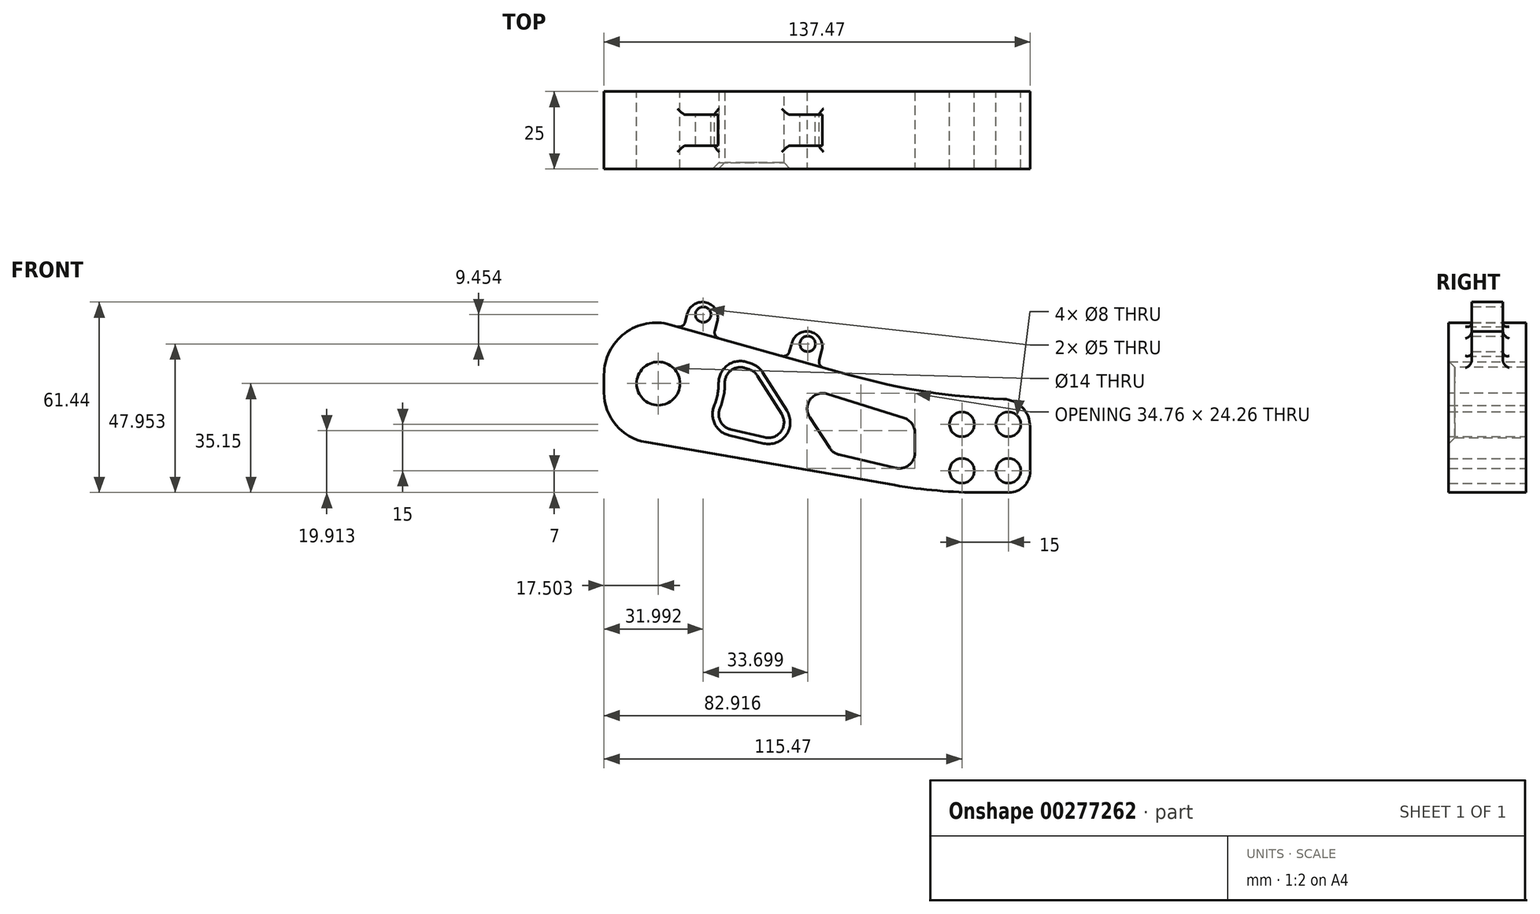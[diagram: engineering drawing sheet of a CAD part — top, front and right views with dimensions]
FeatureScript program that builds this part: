
annotation { "Feature Type Name" : "Feature", "Feature Type Description" : "" }
export const myFeature = defineFeature(function(context is Context, id is Id, definition is map)
    precondition{}
    {
        {
            var Q0;
            Q0=qCreatedBy(makeId("Front.planeOp"),FACE);
            var sketch = newSketch(context, id + "F0", { "sketchPlane" : qUnion([Q0])});
            skLineSegment(sketch, "E0.bottom", {"start": v(15, 15) * mm, "end": v(-15, 15) * mm});
            skLineSegment(sketch, "E0.top", {"start": v(15, -15) * mm, "end": v(-15, -15) * mm});
            skLineSegment(sketch, "E0.left", {"start": v(15, 15) * mm, "end": v(15, -15) * mm});
            skLineSegment(sketch, "E0.right", {"start": v(-15, 15) * mm, "end": v(-15, -15) * mm});
            skPoint(sketch, "E0.middle", {"position": v(0, 0) * mm});
            skCircle(sketch, "E1", {"center": v(-7, 7) * mm, "radius": 4 * mm});
            skCircle(sketch, "E2.0.1.0", {"center": v(-7, -8) * mm, "radius": 4 * mm});
            skCircle(sketch, "E2.1.0.0", {"center": v(8, 7) * mm, "radius": 4 * mm});
            skCircle(sketch, "E2.1.1.0", {"center": v(8, -8) * mm, "radius": 4 * mm});
            skLineSegment(sketch, "E2.direction1", {"start": v(-7, 7) * mm, "end": v(8, 7) * mm, "construction": true});
            skLineSegment(sketch, "E2.direction2", {"start": v(-7, 7) * mm, "end": v(-7, -8) * mm, "construction": true});
            skLineSegment(sketch, "E3", {"start": v(-15, 15) * mm, "end": v(-122.47, 45.15) * mm});
            skLineSegment(sketch, "E4", {"start": v(-122.47, 45.15) * mm, "end": v(-122.47, 3.55) * mm});
            skLineSegment(sketch, "E5", {"start": v(-122.47, 3.55) * mm, "end": v(-15, -15) * mm});
            skCircle(sketch, "E6", {"center": v(-104.97, 20.15) * mm, "radius": 7 * mm});
            skLineSegment(sketch, "E7", {"start": v(-96.91, 37.98) * mm, "end": v(-94.21, 47.6) * mm});
            skLineSegment(sketch, "E8", {"start": v(-94.21, 47.6) * mm, "end": v(-84.58, 44.9) * mm});
            skLineSegment(sketch, "E9", {"start": v(-84.58, 44.9) * mm, "end": v(-87.28, 35.28) * mm});
            skLineSegment(sketch, "E10", {"start": v(-87.28, 35.28) * mm, "end": v(-96.91, 37.98) * mm});
            skLineSegment(sketch, "E11", {"start": v(-63.21, 28.53) * mm, "end": v(-60.51, 38.15) * mm});
            skLineSegment(sketch, "E12", {"start": v(-60.51, 38.15) * mm, "end": v(-50.88, 35.45) * mm});
            skLineSegment(sketch, "E13", {"start": v(-50.88, 35.45) * mm, "end": v(-53.59, 25.83) * mm});
            skSolve(sketch);
        }
        {
            var Q0;
            Q0 = qSketchRegion(id + "F0", true);
            extrude(context, id + "F1", {"entities" : qUnion([Q0]), "depth" : 25 * mm});
        }
        {
            var Q0;
            Q0=makeQuery(id+"F1.opExtrude","SWEPT_EDGE",EDGE,{"disambiguationData":[OSD([sQuery(id+"F0.wireOp",EDGE,"E3"),sQuery(id+"F0.wireOp",EDGE,"E4")])]});
            fillet(context, id + "F2", {"entities" : qUnion([Q0]), "radius" : 16.78 * mm, "tangentPropagation" : true, "allowEdgeOverflow" : false});
        }
        {
            var Q0;
            Q0=makeQuery(id+"F1.opExtrude","SWEPT_EDGE",EDGE,{"disambiguationData":[OSD([sQuery(id+"F0.wireOp",EDGE,"E4"),sQuery(id+"F0.wireOp",EDGE,"E5")])]});
            fillet(context, id + "F3", {"entities" : qUnion([Q0]), "radius" : 16.27 * mm, "tangentPropagation" : true, "allowEdgeOverflow" : false});
        }
        {
            var Q0;
            Q0=makeQuery(id+"F1.opExtrude","SWEPT_EDGE",EDGE,{"disambiguationData":[OSD([sQuery(id+"F0.wireOp",EDGE,"E0.bottom"),sQuery(id+"F0.wireOp",EDGE,"E0.right"),sQuery(id+"F0.wireOp",EDGE,"E3")])]});
            fillet(context, id + "F4", {"entities" : qUnion([Q0]), "radius" : 212.2 * mm, "tangentPropagation" : true, "allowEdgeOverflow" : false});
        }
        {
            var Q0;
            Q0=makeQuery(id+"F1.opExtrude","SWEPT_EDGE",EDGE,{"disambiguationData":[OSD([sQuery(id+"F0.wireOp",EDGE,"E0.top"),sQuery(id+"F0.wireOp",EDGE,"E0.right"),sQuery(id+"F0.wireOp",EDGE,"E5")])]});
            fillet(context, id + "F5", {"entities" : qUnion([Q0]), "radius" : 163.8 * mm, "tangentPropagation" : true, "allowEdgeOverflow" : false});
        }
        {
            var Q0;
            Q0=makeQuery(id+"F1.opExtrude","SWEPT_EDGE",EDGE,{"disambiguationData":[OSD([sQuery(id+"F0.wireOp",EDGE,"E0.bottom"),sQuery(id+"F0.wireOp",EDGE,"E0.left")])]});
            fillet(context, id + "F6", {"entities" : qUnion([Q0]), "radius" : 8.93 * mm, "tangentPropagation" : true, "allowEdgeOverflow" : false});
        }
        {
            var Q0;
            Q0=makeQuery(id+"F1.opExtrude","SWEPT_EDGE",EDGE,{"disambiguationData":[OSD([sQuery(id+"F0.wireOp",EDGE,"E0.top"),sQuery(id+"F0.wireOp",EDGE,"E0.left")])]});
            fillet(context, id + "F7", {"entities" : qUnion([Q0]), "radius" : 6.76 * mm, "tangentPropagation" : true, "allowEdgeOverflow" : false});
        }
        {
            var Q0;
            Q0=makeQuery(id+"F1.opExtrude","CAP_FACE",FACE,{"disambiguationData":[OSD([sQuery(id+"F0.wireOp",EDGE,"E0.bottom"),sQuery(id+"F0.wireOp",EDGE,"E0.top"),sQuery(id+"F0.wireOp",EDGE,"E0.left"),sQuery(id+"F0.wireOp",EDGE,"E1"),sQuery(id+"F0.wireOp",EDGE,"E2.0.1.0"),sQuery(id+"F0.wireOp",EDGE,"E2.1.0.0"),sQuery(id+"F0.wireOp",EDGE,"E2.1.1.0"),sQuery(id+"F0.wireOp",EDGE,"E3"),sQuery(id+"F0.wireOp",EDGE,"E4"),sQuery(id+"F0.wireOp",EDGE,"E5"),sQuery(id+"F0.wireOp",EDGE,"E6")])],"isStart":false});
            var sketch = newSketch(context, id + "F8", { "sketchPlane" : qUnion([Q0])});
            skLineSegment(sketch, "E14", {"start": v(-84.84, 27.64) * mm, "end": v(-73.97, 24.22) * mm});
            skLineSegment(sketch, "E15", {"start": v(-22.17, 7.92) * mm, "end": v(-22.17, -8.52) * mm});
            skLineSegment(sketch, "E16", {"start": v(-22.17, -8.52) * mm, "end": v(-48.58, -2.35) * mm});
            skArc(sketch, "E17", {"start": v(-88.2, 6.9) * mm, "mid": v(-83.78, 16.83) * mm, "end": v(-84.84, 27.64) * mm});
            skLineSegment(sketch, "E18", {"start": v(-73.97, 24.22) * mm, "end": v(-58.64, 0) * mm});
            skLineSegment(sketch, "E19", {"start": v(-63.67, 20.98) * mm, "end": v(-48.58, -2.35) * mm});
            skLineSegment(sketch, "E20.trimOffspring", {"start": v(-63.67, 20.98) * mm, "end": v(-22.17, 7.92) * mm});
            skLineSegment(sketch, "E21.trimOffspring", {"start": v(-58.64, 0) * mm, "end": v(-88.2, 6.9) * mm});
            skSolve(sketch);
        }
        {
            var Q0;
            Q0 = qSketchRegion(id + "F8", true);
            extrude(context, id + "F9", {"entities" : qUnion([Q0]), "operationType" : NewBodyOperationType.REMOVE, "oppositeDirection" : true, "depth" : 25 * mm});
        }
        {
            var Q0;
            Q0=makeQuery(id+"F9.boolean.opBoolean","COPY",EDGE,{"derivedFrom":makeQuery(id+"F9.opExtrude","SWEPT_EDGE",EDGE,{"disambiguationData":[OSD([sQuery(id+"F8.wireOp",EDGE,"E17"),sQuery(id+"F8.wireOp",EDGE,"E21.trimOffspring")])]})});
            var Q1;
            Q1=makeQuery(id+"F9.boolean.opBoolean","COPY",EDGE,{"derivedFrom":makeQuery(id+"F9.opExtrude","SWEPT_EDGE",EDGE,{"disambiguationData":[OSD([sQuery(id+"F8.wireOp",EDGE,"E14"),sQuery(id+"F8.wireOp",EDGE,"E17")])]})});
            var Q2;
            Q2=makeQuery(id+"F9.boolean.opBoolean","COPY",EDGE,{"derivedFrom":makeQuery(id+"F9.opExtrude","SWEPT_EDGE",EDGE,{"disambiguationData":[OSD([sQuery(id+"F8.wireOp",EDGE,"E14"),sQuery(id+"F8.wireOp",EDGE,"E18")])]})});
            var Q3;
            Q3=makeQuery(id+"F9.boolean.opBoolean","COPY",EDGE,{"derivedFrom":makeQuery(id+"F9.opExtrude","SWEPT_EDGE",EDGE,{"disambiguationData":[OSD([sQuery(id+"F8.wireOp",EDGE,"E18"),sQuery(id+"F8.wireOp",EDGE,"E21.trimOffspring")])]})});
            var Q4;
            Q4=makeQuery(id+"F9.boolean.opBoolean","COPY",EDGE,{"derivedFrom":makeQuery(id+"F9.opExtrude","SWEPT_EDGE",EDGE,{"disambiguationData":[OSD([sQuery(id+"F8.wireOp",EDGE,"E19"),sQuery(id+"F8.wireOp",EDGE,"E20.trimOffspring")])]})});
            var Q5;
            Q5=makeQuery(id+"F9.boolean.opBoolean","COPY",EDGE,{"derivedFrom":makeQuery(id+"F9.opExtrude","SWEPT_EDGE",EDGE,{"disambiguationData":[OSD([sQuery(id+"F8.wireOp",EDGE,"E16"),sQuery(id+"F8.wireOp",EDGE,"E19")])]})});
            var Q6;
            Q6=makeQuery(id+"F9.boolean.opBoolean","COPY",EDGE,{"derivedFrom":makeQuery(id+"F9.opExtrude","SWEPT_EDGE",EDGE,{"disambiguationData":[OSD([sQuery(id+"F8.wireOp",EDGE,"E15"),sQuery(id+"F8.wireOp",EDGE,"E16")])]})});
            var Q7;
            Q7=makeQuery(id+"F9.boolean.opBoolean","COPY",EDGE,{"derivedFrom":makeQuery(id+"F9.opExtrude","SWEPT_EDGE",EDGE,{"disambiguationData":[OSD([sQuery(id+"F8.wireOp",EDGE,"E15"),sQuery(id+"F8.wireOp",EDGE,"E20.trimOffspring")])]})});
            fillet(context, id + "F10", {"entities" : qUnion([Q0, Q1, Q2, Q3, Q4, Q5, Q6, Q7]), "radius" : 5 * mm, "tangentPropagation" : true, "allowEdgeOverflow" : false});
        }
        {
            var Q0;
            Q0=makeQuery(id+"F10.opFillet","BLEND_EDGE",EDGE,{"blendedFrom":[makeQuery(id+"F9.boolean.opBoolean","COPY",EDGE,{"derivedFrom":makeQuery(id+"F9.opExtrude","SWEPT_EDGE",EDGE,{"disambiguationData":[OSD([sQuery(id+"F8.wireOp",EDGE,"E14"),sQuery(id+"F8.wireOp",EDGE,"E17")])]})}),makeQuery(id+"F1.opExtrude","CAP_FACE",FACE,{"disambiguationData":[OSD([sQuery(id+"F0.wireOp",EDGE,"E0.bottom"),sQuery(id+"F0.wireOp",EDGE,"E0.top"),sQuery(id+"F0.wireOp",EDGE,"E0.left"),sQuery(id+"F0.wireOp",EDGE,"E1"),sQuery(id+"F0.wireOp",EDGE,"E2.0.1.0"),sQuery(id+"F0.wireOp",EDGE,"E2.1.0.0"),sQuery(id+"F0.wireOp",EDGE,"E2.1.1.0"),sQuery(id+"F0.wireOp",EDGE,"E3"),sQuery(id+"F0.wireOp",EDGE,"E4"),sQuery(id+"F0.wireOp",EDGE,"E5"),sQuery(id+"F0.wireOp",EDGE,"E6")])],"isStart":false})],"blendedInto":[makeQuery(id+"F1.opExtrude","CAP_FACE",FACE,{"disambiguationData":[OSD([sQuery(id+"F0.wireOp",EDGE,"E0.bottom"),sQuery(id+"F0.wireOp",EDGE,"E0.top"),sQuery(id+"F0.wireOp",EDGE,"E0.left"),sQuery(id+"F0.wireOp",EDGE,"E1"),sQuery(id+"F0.wireOp",EDGE,"E2.0.1.0"),sQuery(id+"F0.wireOp",EDGE,"E2.1.0.0"),sQuery(id+"F0.wireOp",EDGE,"E2.1.1.0"),sQuery(id+"F0.wireOp",EDGE,"E3"),sQuery(id+"F0.wireOp",EDGE,"E4"),sQuery(id+"F0.wireOp",EDGE,"E5"),sQuery(id+"F0.wireOp",EDGE,"E6")])],"isStart":false})]});
            var Q1;
            Q1=makeQuery(id+"F9.boolean.opBoolean","COPY",EDGE,{"derivedFrom":makeQuery(id+"F9.opExtrude","CAP_EDGE",EDGE,{"disambiguationData":[OSD([sQuery(id+"F8.wireOp",EDGE,"E20.trimOffspring")])],"isStart":true})});
            var Q2;
            Q2=makeQuery(id+"F9.boolean.opBoolean","COPY",EDGE,{"derivedFrom":makeQuery(id+"F9.opExtrude","CAP_EDGE",EDGE,{"disambiguationData":[OSD([sQuery(id+"F8.wireOp",EDGE,"E20.trimOffspring")])],"isStart":false})});
            var Q3;
            Q3=makeQuery(id+"F9.boolean.opBoolean","COPY",EDGE,{"derivedFrom":makeQuery(id+"F9.opExtrude","CAP_EDGE",EDGE,{"disambiguationData":[OSD([sQuery(id+"F8.wireOp",EDGE,"E18")])],"isStart":false})});
            chamfer(context, id + "F11", {"entities" : qUnion([Q0, Q1, Q2, Q3]), "width" : 2 * mm, "tangentPropagation" : true});
        }
        {
            var Q0;
            Q0=makeQuery(id+"F1.opExtrude","CAP_FACE",FACE,{"disambiguationData":[OSD([sQuery(id+"F0.wireOp",EDGE,"E0.bottom"),sQuery(id+"F0.wireOp",EDGE,"E0.top"),sQuery(id+"F0.wireOp",EDGE,"E0.left"),sQuery(id+"F0.wireOp",EDGE,"E1"),sQuery(id+"F0.wireOp",EDGE,"E2.0.1.0"),sQuery(id+"F0.wireOp",EDGE,"E2.1.0.0"),sQuery(id+"F0.wireOp",EDGE,"E2.1.1.0"),sQuery(id+"F0.wireOp",EDGE,"E3"),sQuery(id+"F0.wireOp",EDGE,"E4"),sQuery(id+"F0.wireOp",EDGE,"E5"),sQuery(id+"F0.wireOp",EDGE,"E6"),sQuery(id+"F0.wireOp",EDGE,"E7"),sQuery(id+"F0.wireOp",EDGE,"E8"),sQuery(id+"F0.wireOp",EDGE,"E9"),sQuery(id+"F0.wireOp",EDGE,"E11"),sQuery(id+"F0.wireOp",EDGE,"E12"),sQuery(id+"F0.wireOp",EDGE,"E13")])],"isStart":false});
            var sketch = newSketch(context, id + "F12", { "sketchPlane" : qUnion([Q0])});
            skLineSegment(sketch, "E22", {"start": v(-60.51, 38.15) * mm, "end": v(-63.21, 28.53) * mm});
            skLineSegment(sketch, "E23", {"start": v(-63.21, 28.53) * mm, "end": v(-53.59, 25.83) * mm});
            skLineSegment(sketch, "E24", {"start": v(-53.59, 25.83) * mm, "end": v(-50.88, 35.45) * mm});
            skLineSegment(sketch, "E25", {"start": v(-50.88, 35.45) * mm, "end": v(-60.51, 38.15) * mm});
            skLineSegment(sketch, "E26", {"start": v(-84.58, 44.9) * mm, "end": v(-94.21, 47.6) * mm});
            skLineSegment(sketch, "E27", {"start": v(-94.21, 47.6) * mm, "end": v(-96.91, 37.98) * mm});
            skLineSegment(sketch, "E28", {"start": v(-96.91, 37.98) * mm, "end": v(-87.28, 35.28) * mm});
            skLineSegment(sketch, "E29", {"start": v(-87.28, 35.28) * mm, "end": v(-84.58, 44.9) * mm});
            skSolve(sketch);
        }
        {
            var Q0;
            Q0 = qSketchRegion(id + "F12", true);
            extrude(context, id + "F13", {"entities" : qUnion([Q0]), "operationType" : NewBodyOperationType.REMOVE, "oppositeDirection" : true, "depth" : 7.5 * mm});
        }
        {
            var Q0;
            Q0=makeQuery(id+"F1.opExtrude","CAP_FACE",FACE,{"disambiguationData":[OSD([sQuery(id+"F0.wireOp",EDGE,"E0.bottom"),sQuery(id+"F0.wireOp",EDGE,"E0.top"),sQuery(id+"F0.wireOp",EDGE,"E0.left"),sQuery(id+"F0.wireOp",EDGE,"E1"),sQuery(id+"F0.wireOp",EDGE,"E2.0.1.0"),sQuery(id+"F0.wireOp",EDGE,"E2.1.0.0"),sQuery(id+"F0.wireOp",EDGE,"E2.1.1.0"),sQuery(id+"F0.wireOp",EDGE,"E3"),sQuery(id+"F0.wireOp",EDGE,"E4"),sQuery(id+"F0.wireOp",EDGE,"E5"),sQuery(id+"F0.wireOp",EDGE,"E6"),sQuery(id+"F0.wireOp",EDGE,"E7"),sQuery(id+"F0.wireOp",EDGE,"E8"),sQuery(id+"F0.wireOp",EDGE,"E9"),sQuery(id+"F0.wireOp",EDGE,"E11"),sQuery(id+"F0.wireOp",EDGE,"E12"),sQuery(id+"F0.wireOp",EDGE,"E13")])],"isStart":true});
            var sketch = newSketch(context, id + "F14", { "sketchPlane" : qUnion([Q0])});
            skLineSegment(sketch, "E30", {"start": v(63.21, 28.53) * mm, "end": v(53.59, 25.83) * mm});
            skLineSegment(sketch, "E31", {"start": v(53.59, 25.83) * mm, "end": v(50.88, 35.45) * mm});
            skLineSegment(sketch, "E32", {"start": v(50.88, 35.45) * mm, "end": v(60.51, 38.15) * mm});
            skLineSegment(sketch, "E33", {"start": v(60.51, 38.15) * mm, "end": v(63.21, 28.53) * mm});
            skLineSegment(sketch, "E34", {"start": v(84.58, 44.9) * mm, "end": v(94.21, 47.6) * mm});
            skLineSegment(sketch, "E35", {"start": v(94.21, 47.6) * mm, "end": v(96.91, 37.98) * mm});
            skLineSegment(sketch, "E36", {"start": v(96.91, 37.98) * mm, "end": v(87.28, 35.28) * mm});
            skLineSegment(sketch, "E37", {"start": v(87.28, 35.28) * mm, "end": v(84.58, 44.9) * mm});
            skSolve(sketch);
        }
        {
            var Q0;
            Q0 = qSketchRegion(id + "F14", true);
            extrude(context, id + "F15", {"entities" : qUnion([Q0]), "operationType" : NewBodyOperationType.REMOVE, "oppositeDirection" : true, "depth" : 7.5 * mm});
        }
        {
            var Q0;
            Q0=makeQuery(id+"F15.boolean.opBoolean","COPY",EDGE,{"derivedFrom":makeQuery(id+"F15.opExtrude","CAP_EDGE",EDGE,{"disambiguationData":[OSD([sQuery(id+"F14.wireOp",EDGE,"E30")])],"isStart":false})});
            var Q1;
            Q1=makeQuery(id+"F1.opExtrude","SWEPT_EDGE",EDGE,{"disambiguationData":[OSD([sQuery(id+"F0.wireOp",EDGE,"E3"),sQuery(id+"F0.wireOp",EDGE,"E13")])]});
            var Q2;
            Q2=makeQuery(id+"F13.boolean.opBoolean","COPY",EDGE,{"derivedFrom":makeQuery(id+"F13.opExtrude","CAP_EDGE",EDGE,{"disambiguationData":[OSD([sQuery(id+"F12.wireOp",EDGE,"E23")])],"isStart":false})});
            var Q3;
            Q3=makeQuery(id+"F1.opExtrude","SWEPT_EDGE",EDGE,{"disambiguationData":[OSD([sQuery(id+"F0.wireOp",EDGE,"E3"),sQuery(id+"F0.wireOp",EDGE,"E11")])]});
            var Q4;
            Q4=makeQuery(id+"F1.opExtrude","SWEPT_EDGE",EDGE,{"disambiguationData":[OSD([sQuery(id+"F0.wireOp",EDGE,"E3"),sQuery(id+"F0.wireOp",EDGE,"E9"),sQuery(id+"F0.wireOp",EDGE,"E10")])]});
            var Q5;
            Q5=makeQuery(id+"F13.boolean.opBoolean","COPY",EDGE,{"derivedFrom":makeQuery(id+"F13.opExtrude","CAP_EDGE",EDGE,{"disambiguationData":[OSD([sQuery(id+"F12.wireOp",EDGE,"E28")])],"isStart":false})});
            var Q6;
            Q6=makeQuery(id+"F15.boolean.opBoolean","COPY",EDGE,{"derivedFrom":makeQuery(id+"F15.opExtrude","CAP_EDGE",EDGE,{"disambiguationData":[OSD([sQuery(id+"F14.wireOp",EDGE,"E36")])],"isStart":false})});
            var Q7;
            Q7=makeQuery(id+"F1.opExtrude","SWEPT_EDGE",EDGE,{"disambiguationData":[OSD([sQuery(id+"F0.wireOp",EDGE,"E3"),sQuery(id+"F0.wireOp",EDGE,"E7"),sQuery(id+"F0.wireOp",EDGE,"E10")])]});
            fillet(context, id + "F16", {"entities" : qUnion([Q0, Q1, Q2, Q3, Q4, Q5, Q6, Q7]), "radius" : 2 * mm, "tangentPropagation" : true, "allowEdgeOverflow" : false});
        }
        {
            var Q0;
            Q0=makeQuery(id+"F15.boolean.opBoolean","COPY",FACE,{"derivedFrom":makeQuery(id+"F15.opExtrude","CAP_FACE",FACE,{"disambiguationData":[OSD([sQuery(id+"F14.wireOp",EDGE,"E30"),sQuery(id+"F14.wireOp",EDGE,"E31"),sQuery(id+"F14.wireOp",EDGE,"E32"),sQuery(id+"F14.wireOp",EDGE,"E33")])],"isStart":false})});
            var sketch = newSketch(context, id + "F17", { "sketchPlane" : qUnion([Q0])});
            skCircle(sketch, "E38", {"center": v(56.78, 32.95) * mm, "radius": 2.5 * mm});
            skPoint(sketch, "E38.centerSnap0", {"position": v(61.97, 32.95) * mm});
            skCircle(sketch, "E39", {"center": v(90.48, 42.4) * mm, "radius": 2.5 * mm});
            skSolve(sketch);
        }
        {
            var Q0;
            Q0 = qSketchRegion(id + "F17", true);
            extrude(context, id + "F18", {"entities" : qUnion([Q0]), "operationType" : NewBodyOperationType.REMOVE, "oppositeDirection" : true, "depth" : 25 * mm});
        }
        {
            var Q0;
            Q0=makeQuery(id+"F1.opExtrude","SWEPT_EDGE",EDGE,{"disambiguationData":[OSD([sQuery(id+"F0.wireOp",EDGE,"E8"),sQuery(id+"F0.wireOp",EDGE,"E9")])]});
            var Q1;
            Q1=makeQuery(id+"F1.opExtrude","SWEPT_EDGE",EDGE,{"disambiguationData":[OSD([sQuery(id+"F0.wireOp",EDGE,"E7"),sQuery(id+"F0.wireOp",EDGE,"E8")])]});
            var Q2;
            Q2=makeQuery(id+"F1.opExtrude","SWEPT_EDGE",EDGE,{"disambiguationData":[OSD([sQuery(id+"F0.wireOp",EDGE,"E12"),sQuery(id+"F0.wireOp",EDGE,"E13")])]});
            var Q3;
            Q3=makeQuery(id+"F1.opExtrude","SWEPT_EDGE",EDGE,{"disambiguationData":[OSD([sQuery(id+"F0.wireOp",EDGE,"E11"),sQuery(id+"F0.wireOp",EDGE,"E12")])]});
            fillet(context, id + "F19", {"entities" : qUnion([Q0, Q1, Q2, Q3]), "radius" : 5 * mm, "tangentPropagation" : true, "allowEdgeOverflow" : false});
        }
    });
